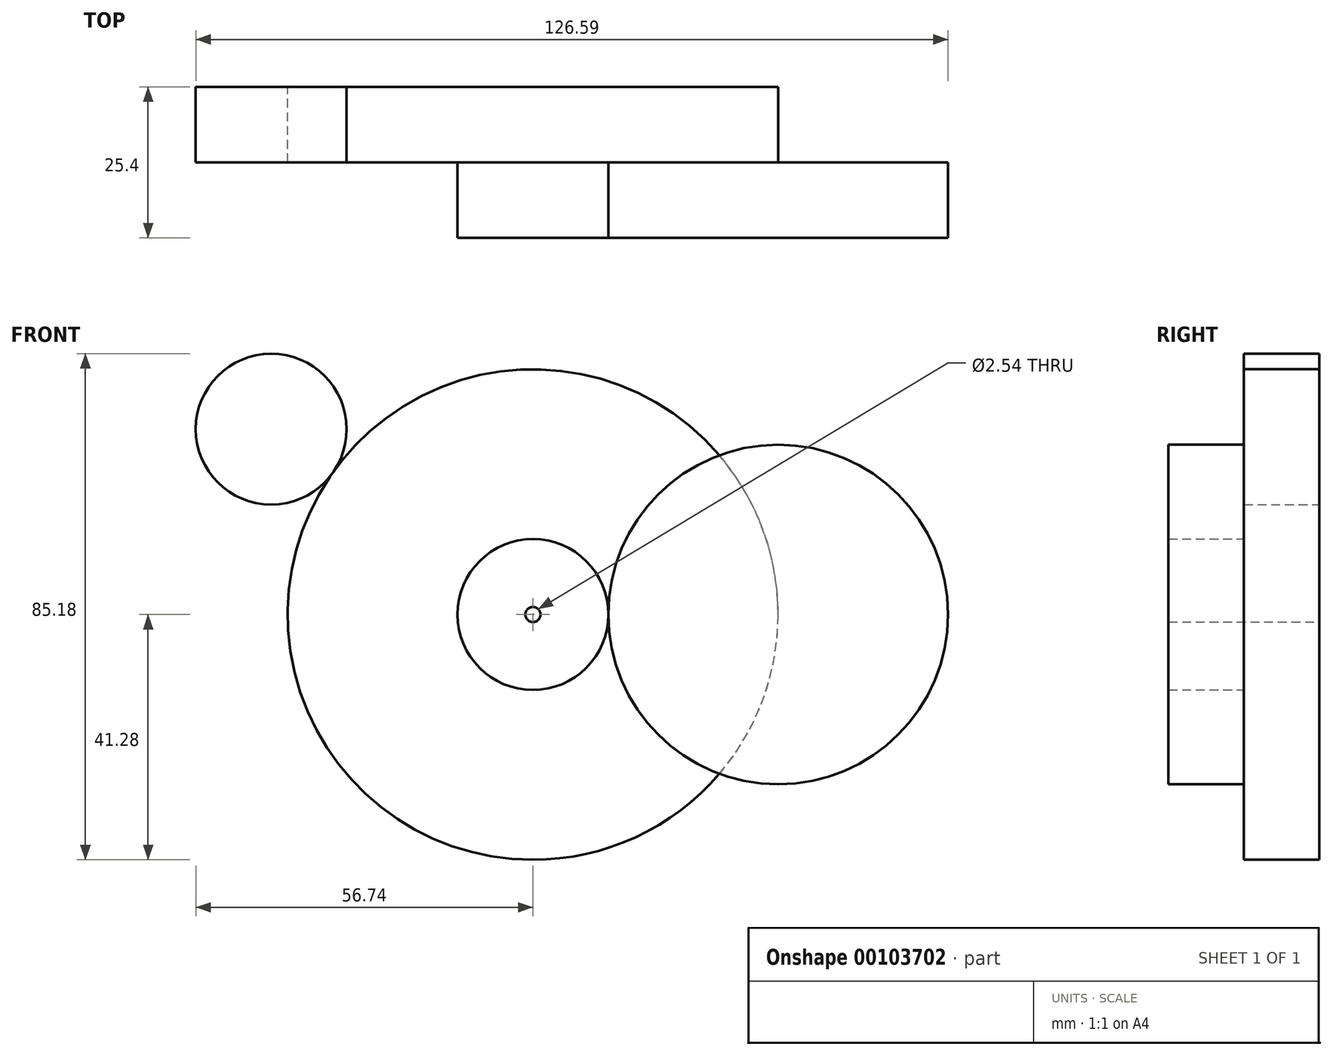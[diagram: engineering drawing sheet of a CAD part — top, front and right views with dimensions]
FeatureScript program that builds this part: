
annotation { "Feature Type Name" : "Feature", "Feature Type Description" : "" }
export const myFeature = defineFeature(function(context is Context, id is Id, definition is map)
    precondition{}
    {
        {
            var Q0;
            Q0=qCreatedBy(makeId("Front.planeOp"),FACE);
            var sketch = newSketch(context, id + "F0", { "sketchPlane" : qUnion([Q0])});
            skCircle(sketch, "E0", {"center": v(0, 0) * mm, "radius": 41.28 * mm});
            skCircle(sketch, "E1", {"center": v(0, 0) * mm, "radius": 1.27 * mm});
            skCircle(sketch, "E2", {"center": v(-44.04, 31.2) * mm, "radius": 12.7 * mm});
            skSolve(sketch);
        }
        {
            var Q0;
            Q0 = qSketchRegion(id + "F0", true);
            extrude(context, id + "F1", {"entities" : qUnion([Q0]), "depth" : 12.7 * mm});
        }
        {
            var Q0;
            Q0=makeQuery(id+"F1.opExtrude","CAP_FACE",FACE,{"disambiguationData":[OSD([sQuery(id+"F0.wireOp",EDGE,"E0"),sQuery(id+"F0.wireOp",EDGE,"E1")])],"isStart":false});
            var sketch = newSketch(context, id + "F2", { "sketchPlane" : qUnion([Q0])});
            skCircle(sketch, "E3", {"center": v(0, 0) * mm, "radius": 12.7 * mm});
            skCircle(sketch, "E4", {"center": v(41.28, 0) * mm, "radius": 28.58 * mm});
            skSolve(sketch);
        }
        {
            var Q0;
            Q0=makeQuery(id+"F2.imprint","IMPRINT",FACE,{"disambiguationData":[TD([[makeQuery(id+"F2.imprint","IMPRINT",EDGE,{"derivedFrom":sQuery(id+"F2.wireOp",EDGE,"E3")}),1.0]])]});
            extrude(context, id + "F3", {"entities" : qUnion([Q0]), "operationType" : NewBodyOperationType.ADD, "depth" : 12.7 * mm});
        }
        {
            var Q0;
            {var subQ0=sQuery(id+"F2.wireOp",EDGE,"E4");var subQ1=makeQuery(id+"F1.opExtrude","CAP_EDGE",EDGE,{"disambiguationData":[OSD([sQuery(id+"F0.wireOp",EDGE,"E0")])],"isStart":false});var subQ2=makeQuery(id+"F2.imprint","INTERSECT",VERTEX,{"disambiguationData":[OD(0.0)],"derivedFrom":[subQ1,subQ0]});Q0=makeQuery(id+"F2.imprint","IMPRINT",FACE,{"disambiguationData":[TD([[makeQuery(id+"F2.imprint","IMPRINT",EDGE,{"disambiguationData":[TD([[subQ2,1.0]])],"derivedFrom":subQ0}),1.0]])]});}
            var Q1;
            {var subQ0=sQuery(id+"F2.wireOp",EDGE,"E4");var subQ1=makeQuery(id+"F2.imprint","INTERSECT",VERTEX,{"derivedFrom":[sQuery(id+"F2.wireOp",EDGE,"E3"),subQ0]});Q1=makeQuery(id+"F2.imprint","IMPRINT",FACE,{"disambiguationData":[TD([[makeQuery(id+"F2.imprint","IMPRINT",EDGE,{"disambiguationData":[TD([[subQ1,1.0]])],"derivedFrom":subQ0}),1.0]])]});}
            extrude(context, id + "F4", {"entities" : qUnion([Q0, Q1]), "depth" : 12.7 * mm});
        }
    });
